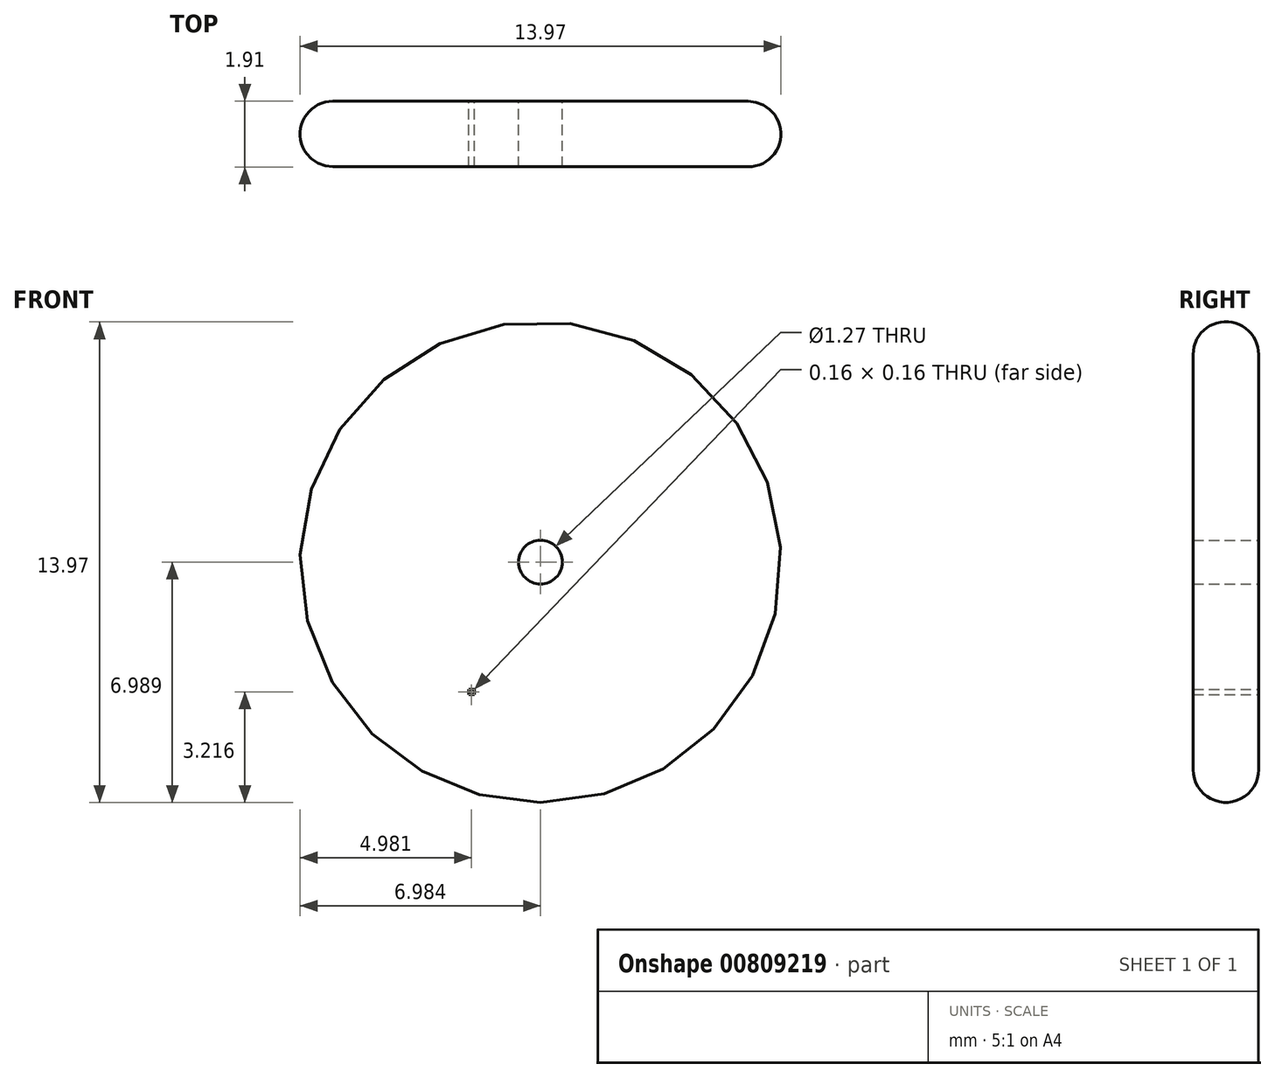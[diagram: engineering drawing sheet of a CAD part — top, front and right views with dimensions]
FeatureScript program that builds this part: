
annotation { "Feature Type Name" : "Feature", "Feature Type Description" : "" }
export const myFeature = defineFeature(function(context is Context, id is Id, definition is map)
    precondition{}
    {
        {
            var Q0;
            Q0=qCreatedBy(makeId("Front.planeOp"),FACE);
            var sketch = newSketch(context, id + "F0", { "sketchPlane" : qUnion([Q0])});
            skCircle(sketch, "E0", {"center": v(-56.43, 38.39) * mm, "radius": 6.99 * mm});
            skCircle(sketch, "E1", {"center": v(-56.43, 38.39) * mm, "radius": 0.64 * mm});
            skLineSegment(sketch, "E2.bottom", {"start": v(-58.51, 34.7) * mm, "end": v(-58.35, 34.7) * mm});
            skLineSegment(sketch, "E2.top", {"start": v(-58.51, 34.54) * mm, "end": v(-58.35, 34.54) * mm});
            skLineSegment(sketch, "E2.left", {"start": v(-58.51, 34.7) * mm, "end": v(-58.51, 34.54) * mm});
            skLineSegment(sketch, "E2.right", {"start": v(-58.35, 34.7) * mm, "end": v(-58.35, 34.54) * mm});
            skSolve(sketch);
        }
        {
            var Q0;
            Q0=makeQuery(id+"F0.imprint","IMPRINT",FACE,{"disambiguationData":[TD([[makeQuery(id+"F0.imprint","IMPRINT",EDGE,{"derivedFrom":sQuery(id+"F0.wireOp",EDGE,"E0")}),1.0]])]});
            extrude(context, id + "F1", {"entities" : qUnion([Q0]), "depth" : 1.9 * mm, "offsetDistance" : 25.4 * mm});
        }
        {
            var Q0;
            Q0=makeQuery(id+"F1.opExtrude","CAP_EDGE",EDGE,{"disambiguationData":[OSD([sQuery(id+"F0.wireOp",EDGE,"E0")])],"isStart":false});
            var Q1;
            Q1=makeQuery(id+"F1.opExtrude","CAP_EDGE",EDGE,{"disambiguationData":[OSD([sQuery(id+"F0.wireOp",EDGE,"E0")])],"isStart":true});
            fillet(context, id + "F2", {"entities" : qUnion([Q0, Q1]), "radius" : 0.95 * mm, "tangentPropagation" : true, "allowEdgeOverflow" : false});
        }
    });
